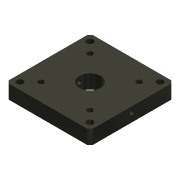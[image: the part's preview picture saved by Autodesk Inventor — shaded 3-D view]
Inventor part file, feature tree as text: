
AUTODESK INVENTOR PART (.ipt)
format: ipt  version: 2019 (Build 230136000, 136)  size: 148,480 bytes
history: native  units: mm
features: sketch x4, projected_geometry x3, extrude x2, hole x2, chamfer x1
ambient origin geometry x8: Origin, YZ Plane, XZ Plane, XY Plane, X Axis, Y Axis, Z Axis, Center Point
bodies: Solid1 (feature_tree)
feature tree (12):
  extrude  "Extrusion1"  Depth=60.0mm
  hole  "Hole1"  [1 undecoded]
  chamfer  "Chamfer1"  Distance=15.0mm
  hole  "Hole2"  [1 undecoded]
  extrude  "Extrusion2"  Depth=10.0mm
  sketch  "Sketch1"  dims[d0=60.0mm d1=60.0mm]
  sketch  "Sketch2"  dims[d2=8.0mm d3=0.0mm d4=35.0mm]
  projected_geometry  "Projected Loop1"
  sketch  "Sketch3"  dims[d5=35.0mm]
  projected_geometry  "Projected Loop2"
  sketch  "Sketch4"  dims[d6=3.9mm d7=6.0mm d8=4.0mm d9=2.0mm d10=90.0deg d11=10.0mm d12=20.594885mm d13=15.0mm d14=2.0mm d15=2.0mm d16=45.0deg d17=50.0mm d18=50.0mm d19=4.65mm d20=6.0mm d21=7.0mm d22=4.0mm d23=90.0deg d24=8.0mm d25=20.594885mm d26=3.0mm d27=4.0mm d28=30.0mm d29=10.0mm d30=0.0mm]
  projected_geometry  "Projected Loop3"
note: 2 required parameter values undecoded (feature->parameter linkage not recoverable at this tier; creation-order binding heuristic only, values carry confidence <= 0.55)
